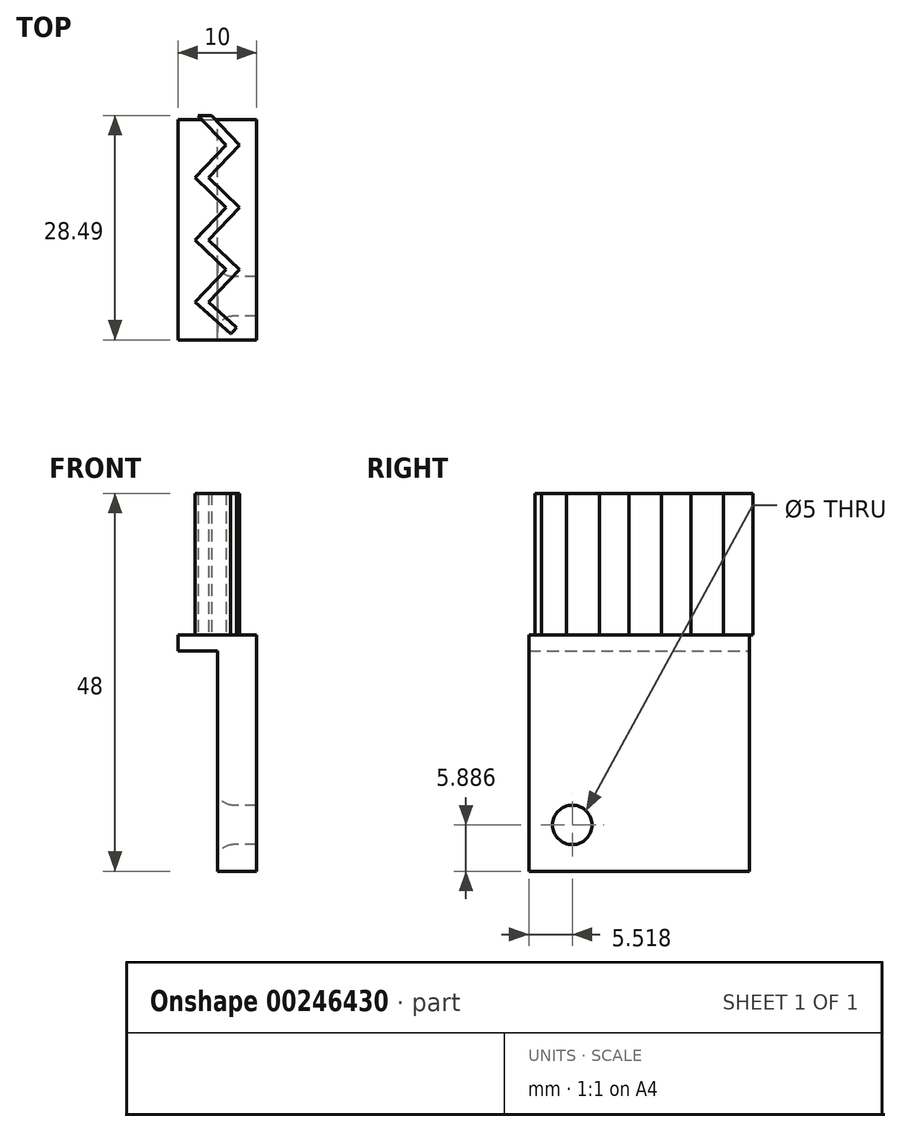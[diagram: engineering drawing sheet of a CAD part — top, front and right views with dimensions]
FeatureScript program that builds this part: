
annotation { "Feature Type Name" : "Feature", "Feature Type Description" : "" }
export const myFeature = defineFeature(function(context is Context, id is Id, definition is map)
    precondition{}
    {
        {
            var Q0;
            Q0=qCreatedBy(makeId("Front.planeOp"),FACE);
            var sketch = newSketch(context, id + "F0", { "sketchPlane" : qUnion([Q0])});
            skLineSegment(sketch, "E0.bottom", {"start": v(-6.25, 8.5) * mm, "end": v(3.75, 8.5) * mm});
            skLineSegment(sketch, "E0.top", {"start": v(-6.25, 6.5) * mm, "end": v(3.75, 6.5) * mm});
            skLineSegment(sketch, "E0.left", {"start": v(-6.25, 8.5) * mm, "end": v(-6.25, 6.5) * mm});
            skLineSegment(sketch, "E0.right", {"start": v(3.75, 8.5) * mm, "end": v(3.75, 6.5) * mm});
            skLineSegment(sketch, "E1.bottom", {"start": v(-1.25, 6.5) * mm, "end": v(3.75, 6.5) * mm});
            skLineSegment(sketch, "E1.top", {"start": v(-1.25, -21.5) * mm, "end": v(3.75, -21.5) * mm});
            skLineSegment(sketch, "E1.left", {"start": v(-1.25, 6.5) * mm, "end": v(-1.25, -21.5) * mm});
            skLineSegment(sketch, "E1.right", {"start": v(3.75, 6.5) * mm, "end": v(3.75, -21.5) * mm});
            skSolve(sketch);
        }
        {
            var Q0;
            Q0 = qSketchRegion(id + "F0", true);
            var Q1;
            Q1 = qSketchRegion(id + "F2", true);
            extrude(context, id + "F1", {"entities" : qUnion([Q0, Q1]), "endBound" : BoundingType.SYMMETRIC, "depth" : 28 * mm});
        }
        {
            var Q0;
            Q0=makeQuery(id+"F1.opExtrude","SWEPT_FACE",FACE,{"disambiguationData":[OSD([sQuery(id+"F0.wireOp",EDGE,"E0.bottom")])]});
            var sketch = newSketch(context, id + "F2", { "sketchPlane" : qUnion([Q0])});
            skLineSegment(sketch, "E2", {"start": v(-6.12, 14.5) * mm, "end": v(-6.12, -13.5) * mm, "construction": true});
            skLineSegment(sketch, "E3", {"start": v(-3.72, 14.5) * mm, "end": v(-0.17, 10.74) * mm});
            skLineSegment(sketch, "E4", {"start": v(-0.17, 10.74) * mm, "end": v(-4.12, 6.6) * mm});
            skLineSegment(sketch, "E5", {"start": v(-4.12, 6.6) * mm, "end": v(-0.17, 2.84) * mm});
            skLineSegment(sketch, "E6", {"start": v(-0.17, 2.84) * mm, "end": v(-4.12, -1.3) * mm});
            skLineSegment(sketch, "E7", {"start": v(-4.12, -1.3) * mm, "end": v(-0.17, -5.06) * mm});
            skLineSegment(sketch, "E8", {"start": v(-0.17, -5.06) * mm, "end": v(-4.12, -9.2) * mm});
            skLineSegment(sketch, "E9", {"start": v(-4.12, -9.2) * mm, "end": v(0.43, -13.21) * mm});
            skLineSegment(sketch, "E10", {"start": v(-3.72, 14.5) * mm, "end": v(-1.97, 14.5) * mm});
            skLineSegment(sketch, "E11", {"start": v(3.54, -13.5) * mm, "end": v(2.34, -12.53) * mm});
            skLineSegment(sketch, "E12", {"start": v(-1.97, 14.5) * mm, "end": v(1.58, 10.74) * mm});
            skLineSegment(sketch, "E13", {"start": v(1.58, 10.74) * mm, "end": v(-2.37, 6.6) * mm});
            skLineSegment(sketch, "E14", {"start": v(-2.37, 6.6) * mm, "end": v(1.58, 2.84) * mm});
            skLineSegment(sketch, "E15", {"start": v(1.58, 2.84) * mm, "end": v(-2.37, -1.3) * mm});
            skLineSegment(sketch, "E16", {"start": v(-2.37, -1.3) * mm, "end": v(1.58, -5.06) * mm});
            skLineSegment(sketch, "E17", {"start": v(1.58, -5.06) * mm, "end": v(-2.37, -9.2) * mm});
            skLineSegment(sketch, "E18", {"start": v(-2.37, -9.2) * mm, "end": v(1.17, -12.4) * mm});
            skArc(sketch, "E19", {"start": v(0.43, -13.21) * mm, "mid": v(0.84, -12.84) * mm, "end": v(1.17, -12.4) * mm});
            skSolve(sketch);
        }
        {
            var Q0;
            Q0 = qSketchRegion(id + "F2", true);
            extrude(context, id + "F3", {"entities" : qUnion([Q0]), "operationType" : NewBodyOperationType.ADD, "depth" : 18 * mm});
        }
        {
            var Q0;
            Q0=makeQuery(id+"F1.opExtrude","SWEPT_FACE",FACE,{"disambiguationData":[OSD([sQuery(id+"F0.wireOp",EDGE,"E1.left")])]});
            var sketch = newSketch(context, id + "F4", { "sketchPlane" : qUnion([Q0])});
            skCircle(sketch, "E20", {"center": v(8.48, -15.61) * mm, "radius": 2.5 * mm});
            skSolve(sketch);
        }
        {
            var Q0;
            Q0 = qSketchRegion(id + "F4", true);
            extrude(context, id + "F5", {"entities" : qUnion([Q0]), "operationType" : NewBodyOperationType.REMOVE, "endBound" : BoundingType.SYMMETRIC, "oppositeDirection" : true, "depth" : 10 * mm});
        }
        {
            var Q0;
            Q0=makeQuery(id+"F5.boolean.opBoolean","COPY",EDGE,{"derivedFrom":makeQuery(id+"F5.opExtrude","CAP_EDGE",EDGE,{"disambiguationData":[OSD([sQuery(id+"F4.wireOp",EDGE,"E20")])],"isStart":false})});
            var Q1;
            Q1=makeQuery(id+"F5.boolean.opBoolean","INTERSECT",EDGE,{"derivedFrom":[makeQuery(id+"F1.opExtrude","SWEPT_FACE",FACE,{"disambiguationData":[OSD([sQuery(id+"F0.wireOp",EDGE,"E1.left")])]}),makeQuery(id+"F5.opExtrude","SWEPT_FACE",FACE,{"disambiguationData":[OSD([sQuery(id+"F4.wireOp",EDGE,"E20")])]})]});
            fillet(context, id + "F6", {"entities" : qUnion([Q0, Q1]), "radius" : 2 * mm, "tangentPropagation" : true, "allowEdgeOverflow" : false});
        }
    });
